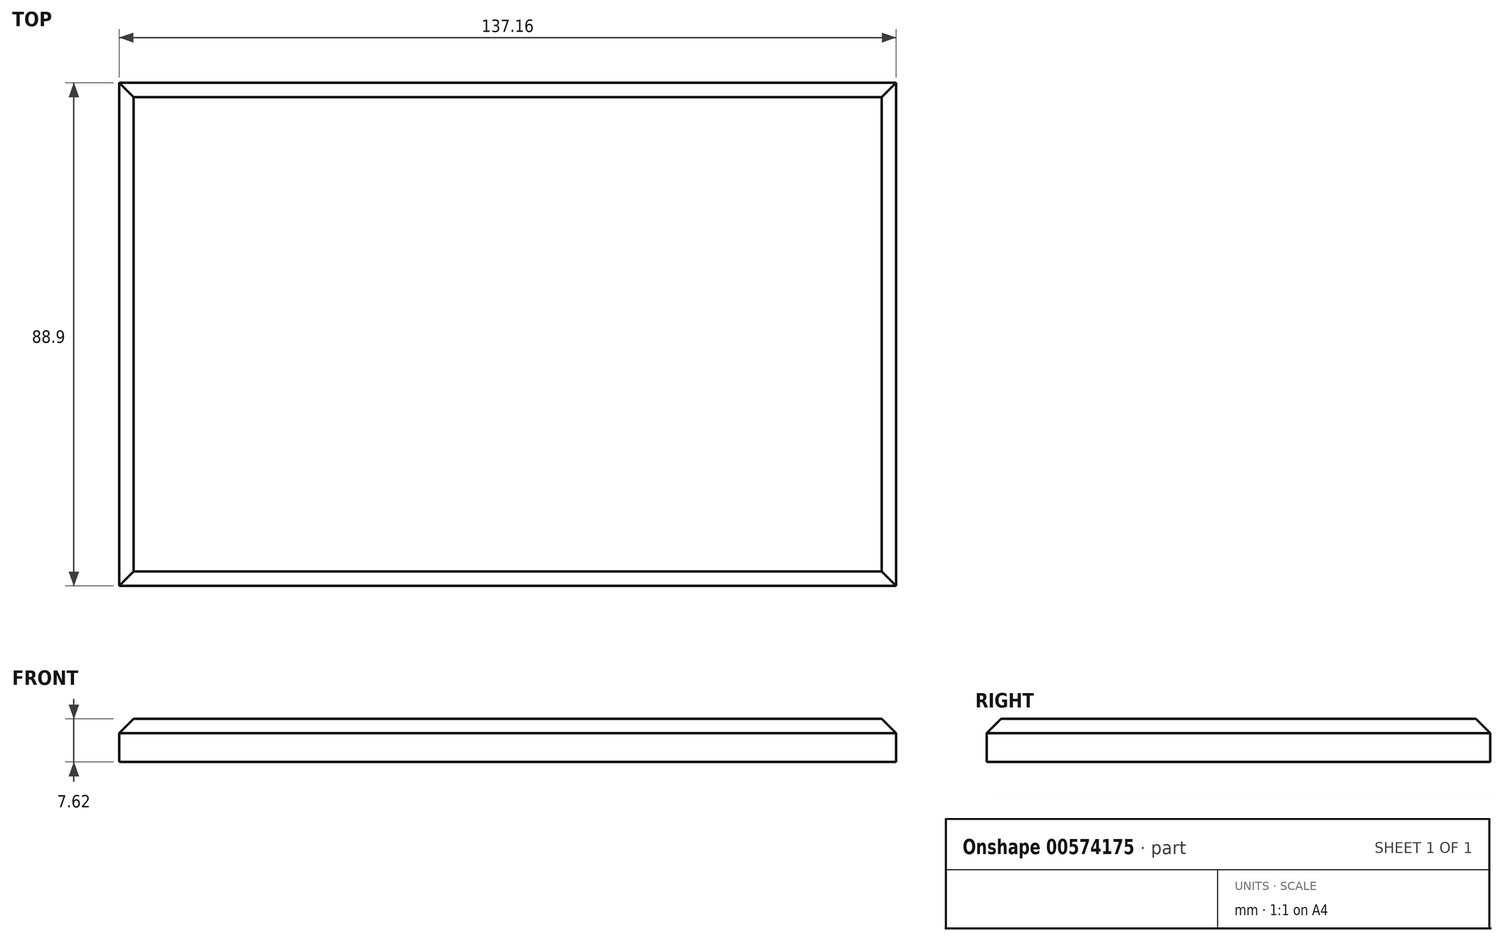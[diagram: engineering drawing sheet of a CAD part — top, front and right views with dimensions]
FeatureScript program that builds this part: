
annotation { "Feature Type Name" : "Feature", "Feature Type Description" : "" }
export const myFeature = defineFeature(function(context is Context, id is Id, definition is map)
    precondition{}
    {
        {
            var Q0;
            Q0=qCreatedBy(makeId("Top.planeOp"),FACE);
            var sketch = newSketch(context, id + "F0", { "sketchPlane" : qUnion([Q0])});
            skLineSegment(sketch, "E0.bottom", {"start": v(-79.92, -27.7) * mm, "end": v(57.24, -27.7) * mm});
            skLineSegment(sketch, "E0.top", {"start": v(-79.92, 61.2) * mm, "end": v(57.24, 61.2) * mm});
            skLineSegment(sketch, "E0.left", {"start": v(-79.92, -27.7) * mm, "end": v(-79.92, 61.2) * mm});
            skLineSegment(sketch, "E0.right", {"start": v(57.24, -27.7) * mm, "end": v(57.24, 61.2) * mm});
            skSolve(sketch);
        }
        {
            var Q0;
            Q0=makeQuery(id+"F0.imprint","IMPRINT",FACE,{"disambiguationData":[TD([[makeQuery(id+"F0.imprint","IMPRINT",EDGE,{"derivedFrom":sQuery(id+"F0.wireOp",EDGE,"E0.bottom")}),1.0]])]});
            extrude(context, id + "F1", {"entities" : qUnion([Q0]), "depth" : 7.62 * mm, "offsetDistance" : 25.4 * mm});
        }
        {
            var Q0;
            Q0=makeQuery(id+"F1.opExtrude","CAP_EDGE",EDGE,{"disambiguationData":[OSD([sQuery(id+"F0.wireOp",EDGE,"E0.left")])],"isStart":false});
            var Q1;
            Q1=makeQuery(id+"F1.opExtrude","CAP_EDGE",EDGE,{"disambiguationData":[OSD([sQuery(id+"F0.wireOp",EDGE,"E0.bottom")])],"isStart":false});
            var Q2;
            Q2=makeQuery(id+"F1.opExtrude","CAP_FACE",FACE,{"disambiguationData":[OSD([sQuery(id+"F0.wireOp",EDGE,"E0.bottom"),sQuery(id+"F0.wireOp",EDGE,"E0.top"),sQuery(id+"F0.wireOp",EDGE,"E0.left"),sQuery(id+"F0.wireOp",EDGE,"E0.right")])],"isStart":false});
            chamfer(context, id + "F2", {"entities" : qUnion([Q0, Q1, Q2]), "width" : 2.54 * mm, "tangentPropagation" : true});
        }
    });
